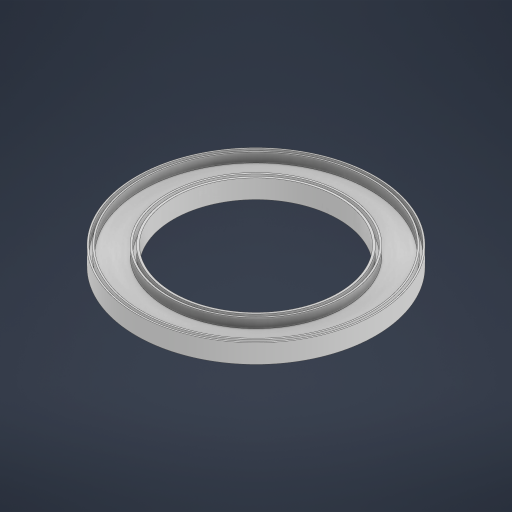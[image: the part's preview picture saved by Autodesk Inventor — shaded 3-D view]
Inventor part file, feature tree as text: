
AUTODESK INVENTOR PART (.ipt)
format: ipt  version: 2024 (Build 280153000, 153)  size: 249,856 bytes
history: native  units: mm
features: extrude x2, sketch x2
ambient origin geometry x8: Origin, YZ Plane, XZ Plane, XY Plane, X Axis, Y Axis, Z Axis, Center Point
bodies: Solid1 (feature_tree)
feature tree (4):
  extrude  "Extrusion1"  Depth=8.0mm TaperAngle=0.0deg
  extrude  "Extrusion2"  [1 undecoded]
  sketch  "Sketch1"  dims[d0=8.0mm d1=0.0mm d2=8.0mm d3=0.0mm]
  sketch  "Sketch2"
note: 1 required parameter value undecoded (feature->parameter linkage not recoverable at this tier; creation-order binding heuristic only, values carry confidence <= 0.55)
